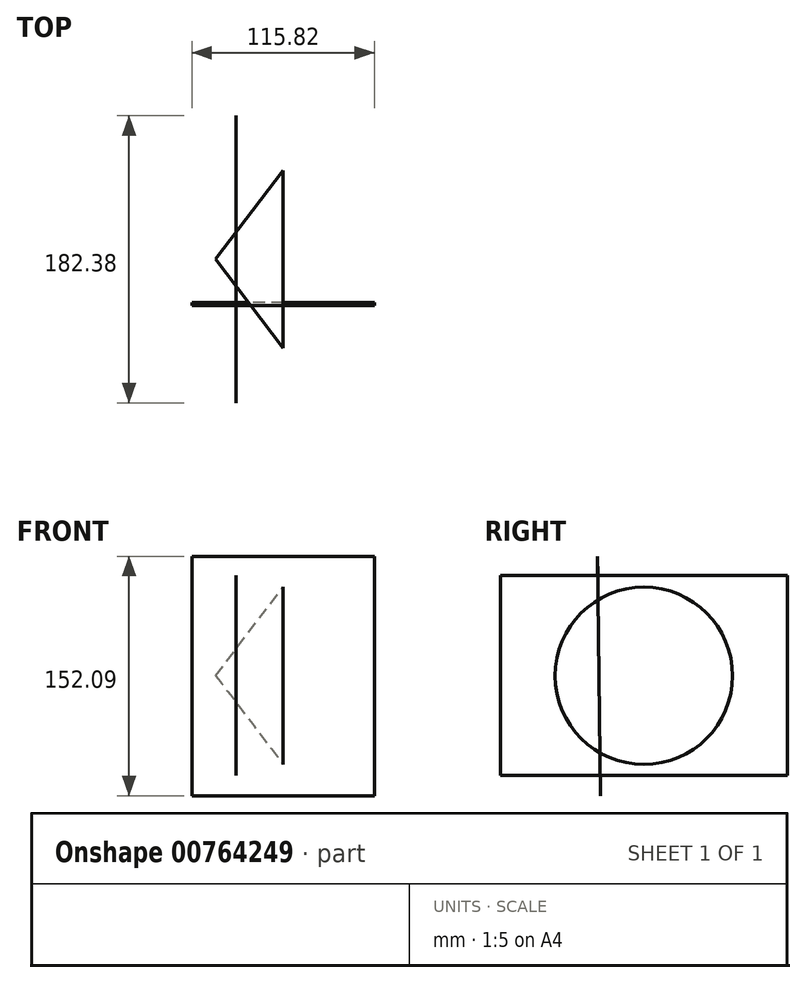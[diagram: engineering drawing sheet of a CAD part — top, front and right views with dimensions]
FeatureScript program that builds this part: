
annotation { "Feature Type Name" : "Feature", "Feature Type Description" : "" }
export const myFeature = defineFeature(function(context is Context, id is Id, definition is map)
    precondition{}
    {
        {
            var Q0;
            Q0=qCreatedBy(makeId("Front.planeOp"),FACE);
            var sketch = newSketch(context, id + "F0", { "sketchPlane" : qUnion([Q0])});
            skLineSegment(sketch, "E0", {"start": v(0, 56.32) * mm, "end": v(-42.86, 0) * mm});
            skLineSegment(sketch, "E1", {"start": v(-42.86, 0) * mm, "end": v(0, 0) * mm});
            skLineSegment(sketch, "E2", {"start": v(0, 0) * mm, "end": v(42.86, 0) * mm});
            skLineSegment(sketch, "E3", {"start": v(42.86, 0) * mm, "end": v(0, 56.32) * mm});
            skSolve(sketch);
        }
        {
            var Q0;
            Q0 = qSketchRegion(id + "F0", true);
            var Q1;
            Q1=sQuery(id+"F0.wireOp",EDGE,"E0");
            var Q2;
            Q2=sQuery(id+"F0.wireOp",EDGE,"E1");
            revolve(context, id + "F1", {"bodyType" : ToolBodyType.SURFACE, "surfaceOperationType" : NewSurfaceOperationType.NEW, "entities" : qUnion([Q0]), "surfaceEntities" : qUnion([Q1]), "axis" : qUnion([Q2]), "revolveType" : RevolveType.FULL});
        }
        {
            var Q0;
            Q0=qCreatedBy(makeId("Right.planeOp"),FACE);
            var sketch = newSketch(context, id + "F2", { "sketchPlane" : qUnion([Q0])});
            skLineSegment(sketch, "E4", {"start": v(-29.4, 75.86) * mm, "end": v(-27.56, -76.23) * mm});
            skSolve(sketch);
        }
        {
            var Q0;
            Q0=sQuery(id+"F2.wireOp",EDGE,"E4");
            extrude(context, id + "F3", {"bodyType" : ToolBodyType.SURFACE, "surfaceEntities" : qUnion([Q0]), "endBound" : BoundingType.SYMMETRIC, "oppositeDirection" : true, "depth" : 115.82 * mm, "offsetDistance" : 25.4 * mm});
        }
        {
            var Q0;
            Q0=qCreatedBy(makeId("Front.planeOp"),FACE);
            var sketch = newSketch(context, id + "F4", { "sketchPlane" : qUnion([Q0])});
            skLineSegment(sketch, "E5", {"start": v(-29.96, 63.7) * mm, "end": v(-29.96, -63.35) * mm});
            skSolve(sketch);
        }
        {
            var Q0;
            Q0=sQuery(id+"F4.wireOp",EDGE,"E5");
            extrude(context, id + "F5", {"bodyType" : ToolBodyType.SURFACE, "surfaceEntities" : qUnion([Q0]), "endBound" : BoundingType.SYMMETRIC, "depth" : 182.37 * mm, "offsetDistance" : 25.4 * mm});
        }
    });
